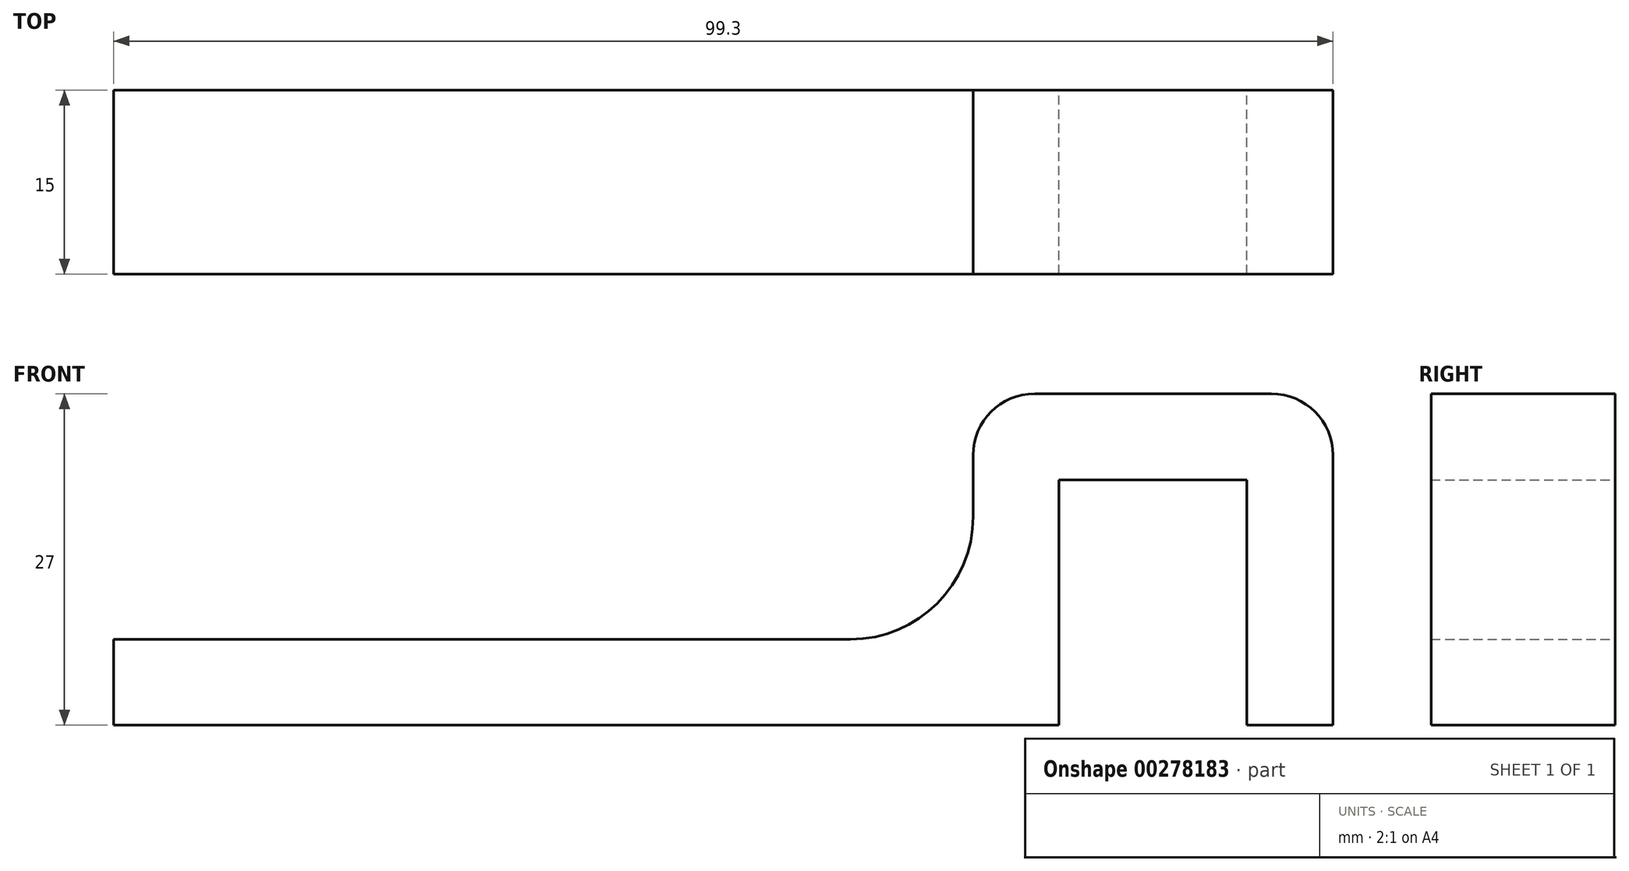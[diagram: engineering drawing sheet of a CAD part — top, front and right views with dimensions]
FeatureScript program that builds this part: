
annotation { "Feature Type Name" : "Feature", "Feature Type Description" : "" }
export const myFeature = defineFeature(function(context is Context, id is Id, definition is map)
    precondition{}
    {
        {
            var Q0;
            Q0=qCreatedBy(makeId("Front.planeOp"),FACE);
            var sketch = newSketch(context, id + "F0", { "sketchPlane" : qUnion([Q0])});
            skLineSegment(sketch, "E0", {"start": v(41.58, 0) * mm, "end": v(41.58, 20) * mm});
            skLineSegment(sketch, "E1", {"start": v(41.58, 20) * mm, "end": v(26.28, 20) * mm});
            skLineSegment(sketch, "E2", {"start": v(26.28, 20) * mm, "end": v(26.28, 0) * mm});
            skLineSegment(sketch, "E3", {"start": v(26.28, 0) * mm, "end": v(-50.72, 0) * mm});
            skLineSegment(sketch, "E4", {"start": v(-50.72, 0) * mm, "end": v(-50.72, 7) * mm});
            skLineSegment(sketch, "E5", {"start": v(-50.72, 7) * mm, "end": v(-45.72, 7) * mm});
            skLineSegment(sketch, "E6", {"start": v(-45.72, 7) * mm, "end": v(-45.72, 7) * mm});
            skLineSegment(sketch, "E7", {"start": v(-45.72, 7) * mm, "end": v(19.28, 7) * mm});
            skLineSegment(sketch, "E8", {"start": v(19.28, 7) * mm, "end": v(19.28, 27) * mm});
            skLineSegment(sketch, "E9", {"start": v(19.28, 27) * mm, "end": v(48.58, 27) * mm});
            skLineSegment(sketch, "E10", {"start": v(48.58, 27) * mm, "end": v(48.58, 0) * mm});
            skLineSegment(sketch, "E11", {"start": v(48.58, 0) * mm, "end": v(41.58, 0) * mm});
            skSolve(sketch);
        }
        {
            var Q0;
            Q0=makeQuery(id+"F0.imprint","IMPRINT",FACE,{"disambiguationData":[TD([[makeQuery(id+"F0.imprint","IMPRINT",EDGE,{"derivedFrom":sQuery(id+"F0.wireOp",EDGE,"E0")}),-1.0]])]});
            extrude(context, id + "F1", {"entities" : qUnion([Q0]), "depth" : 15 * mm});
        }
        {
            var Q0;
            Q0=makeQuery(id+"F1.opExtrude","SWEPT_EDGE",EDGE,{"disambiguationData":[OSD([sQuery(id+"F0.wireOp",EDGE,"E7"),sQuery(id+"F0.wireOp",EDGE,"E8")])]});
            fillet(context, id + "F2", {"entities" : qUnion([Q0]), "radius" : 10 * mm, "tangentPropagation" : true, "allowEdgeOverflow" : false});
        }
        {
            var Q0;
            Q0=makeQuery(id+"F1.opExtrude","SWEPT_EDGE",EDGE,{"disambiguationData":[OSD([sQuery(id+"F0.wireOp",EDGE,"E8"),sQuery(id+"F0.wireOp",EDGE,"E9")])]});
            fillet(context, id + "F3", {"entities" : qUnion([Q0]), "radius" : 5 * mm, "tangentPropagation" : true, "allowEdgeOverflow" : false});
        }
        {
            var Q0;
            Q0=makeQuery(id+"F1.opExtrude","SWEPT_EDGE",EDGE,{"disambiguationData":[OSD([sQuery(id+"F0.wireOp",EDGE,"E9"),sQuery(id+"F0.wireOp",EDGE,"E10")])]});
            fillet(context, id + "F4", {"entities" : qUnion([Q0]), "radius" : 5 * mm, "tangentPropagation" : true, "allowEdgeOverflow" : false});
        }
    });
